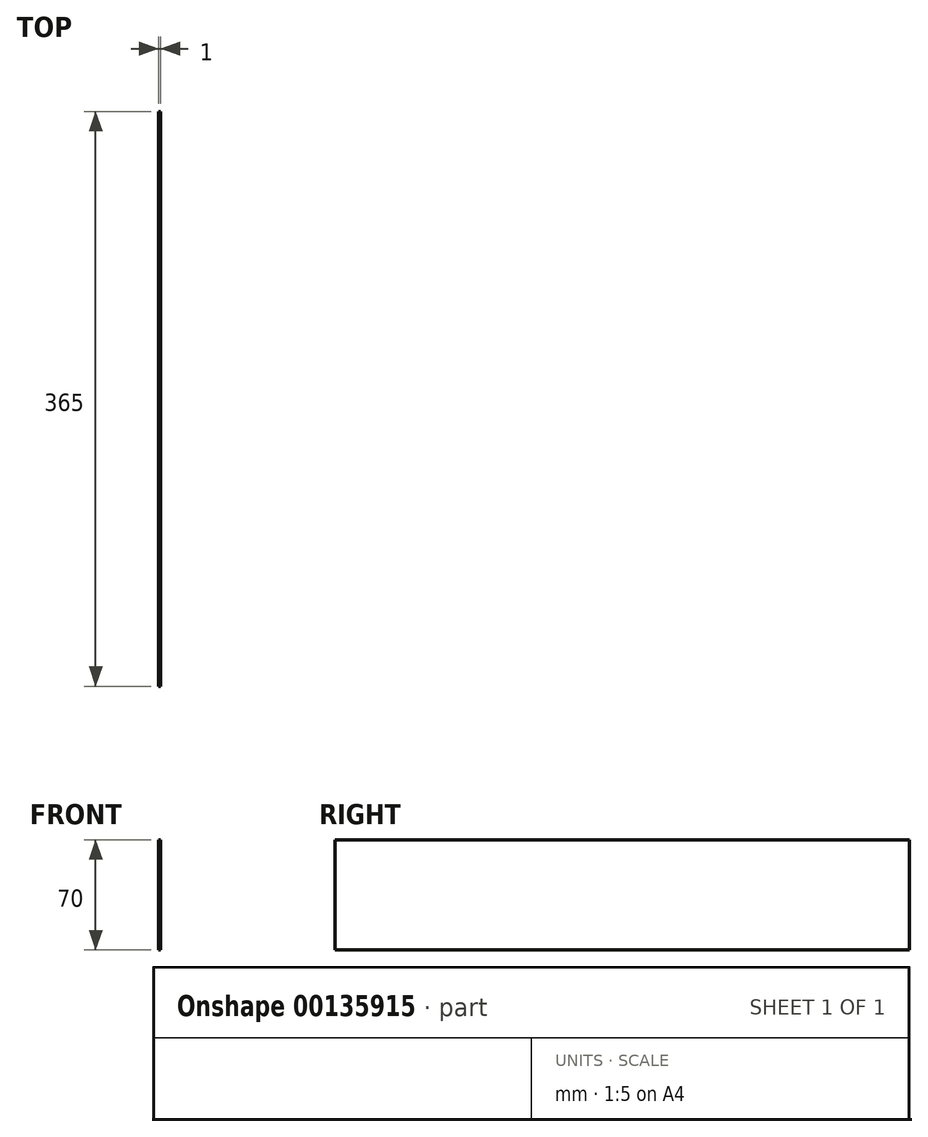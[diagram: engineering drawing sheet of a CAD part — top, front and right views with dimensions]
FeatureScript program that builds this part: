
annotation { "Feature Type Name" : "Feature", "Feature Type Description" : "" }
export const myFeature = defineFeature(function(context is Context, id is Id, definition is map)
    precondition{}
    {
        {
            var Q0;
            Q0=qCreatedBy(makeId("Right.planeOp"),FACE);
            var sketch = newSketch(context, id + "F0", { "sketchPlane" : qUnion([Q0])});
            skLineSegment(sketch, "E0.bottom", {"start": v(0, 0) * mm, "end": v(365, 0) * mm});
            skLineSegment(sketch, "E0.top", {"start": v(0, 70) * mm, "end": v(365, 70) * mm});
            skLineSegment(sketch, "E0.left", {"start": v(0, 0) * mm, "end": v(0, 70) * mm});
            skLineSegment(sketch, "E0.right", {"start": v(365, 0) * mm, "end": v(365, 70) * mm});
            skSolve(sketch);
        }
        {
            var Q0;
            Q0 = qSketchRegion(id + "F0", true);
            extrude(context, id + "F1", {"entities" : qUnion([Q0]), "depth" : 1 * mm});
        }
    });
